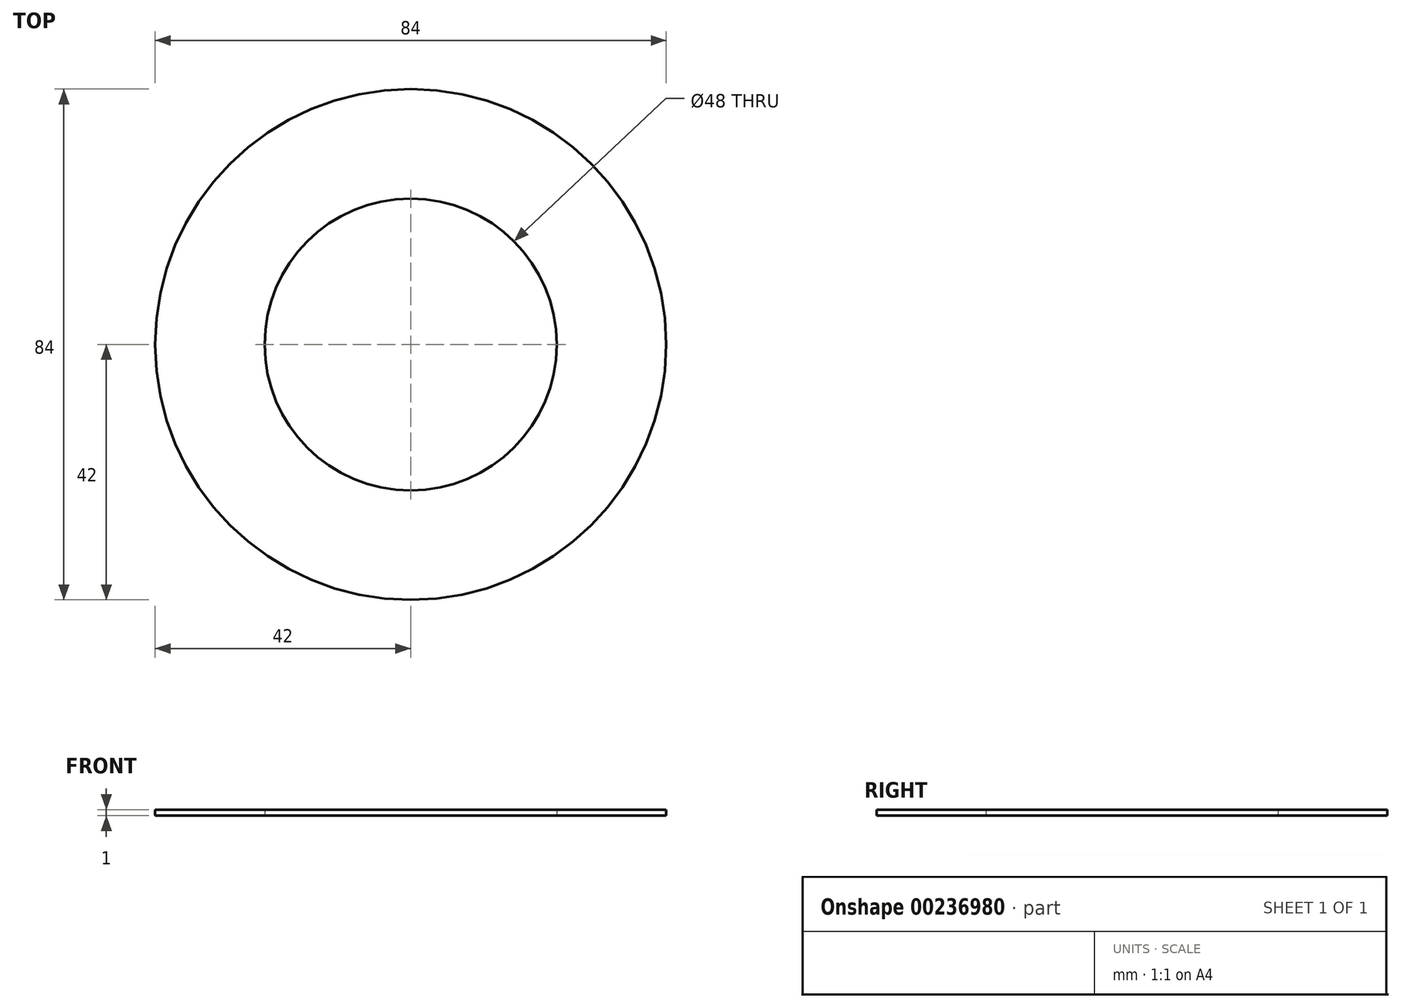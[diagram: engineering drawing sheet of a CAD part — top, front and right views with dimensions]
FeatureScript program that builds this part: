
annotation { "Feature Type Name" : "Feature", "Feature Type Description" : "" }
export const myFeature = defineFeature(function(context is Context, id is Id, definition is map)
    precondition{}
    {
        {
            var Q0;
            Q0=qCreatedBy(makeId("Top.planeOp"),FACE);
            var sketch = newSketch(context, id + "F0", { "sketchPlane" : qUnion([Q0])});
            skCircle(sketch, "E0", {"center": v(0, 0) * mm, "radius": 42 * mm});
            skCircle(sketch, "E1", {"center": v(0, 0) * mm, "radius": 24 * mm});
            skSolve(sketch);
        }
        {
            var Q0;
            Q0 = qSketchRegion(id + "F0", true);
            extrude(context, id + "F1", {"entities" : qUnion([Q0]), "depth" : 1 * mm});
        }
    });
